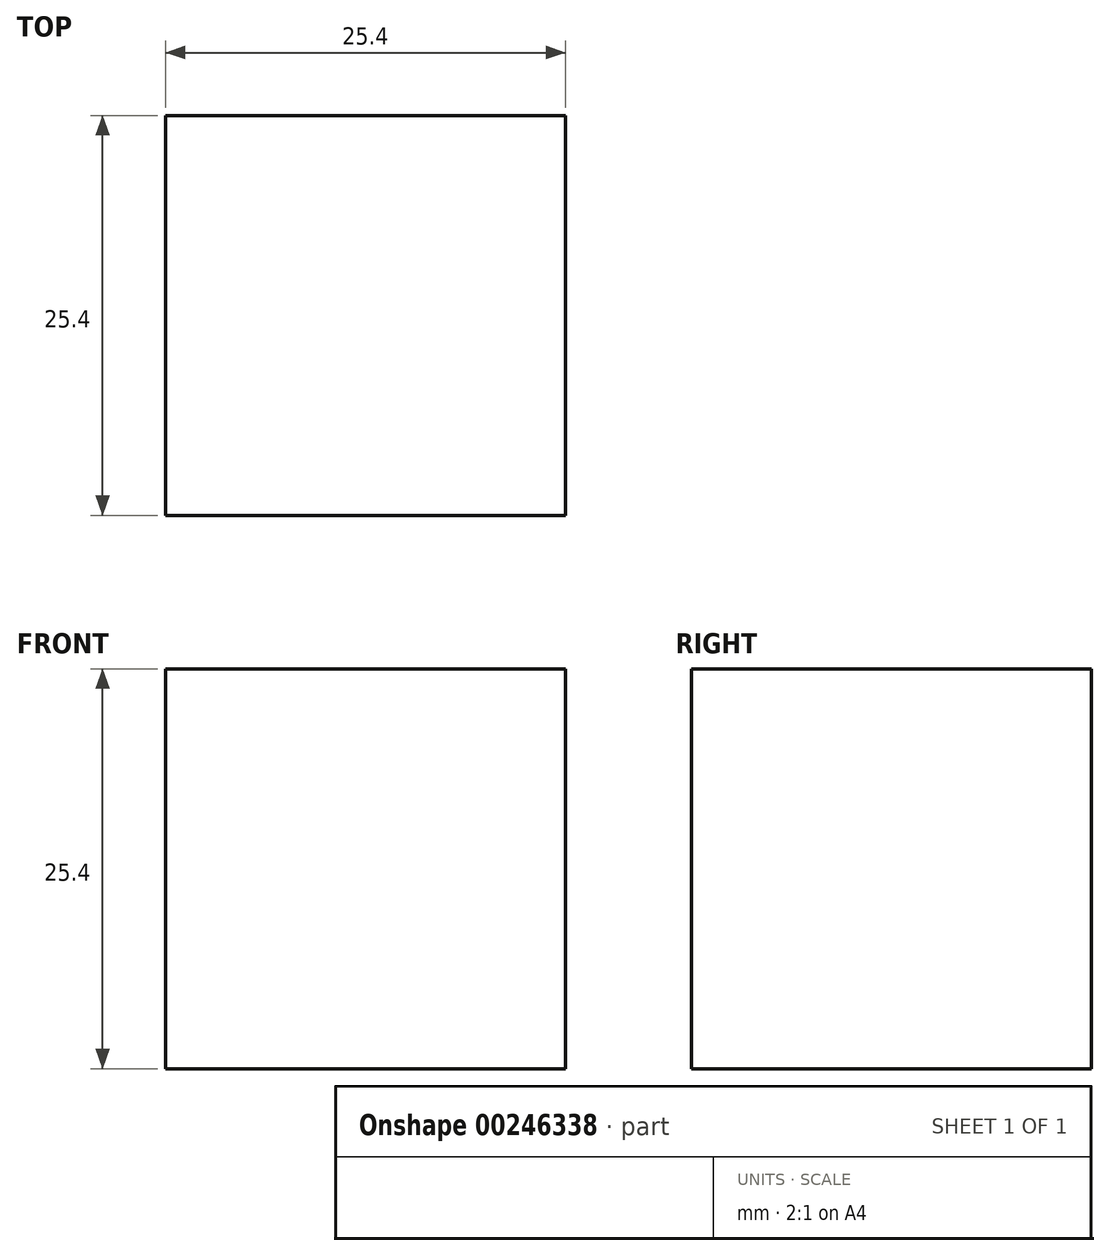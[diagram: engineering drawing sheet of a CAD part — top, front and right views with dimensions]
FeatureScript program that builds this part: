
annotation { "Feature Type Name" : "Feature", "Feature Type Description" : "" }
export const myFeature = defineFeature(function(context is Context, id is Id, definition is map)
    precondition{}
    {
        {
            var Q0;
            Q0=qCreatedBy(makeId("Front.planeOp"),FACE);
            var sketch = newSketch(context, id + "F0", { "sketchPlane" : qUnion([Q0])});
            skLineSegment(sketch, "E0.bottom", {"start": v(-35.63, -10.53) * mm, "end": v(-10.23, -10.53) * mm});
            skLineSegment(sketch, "E0.top", {"start": v(-35.63, -35.93) * mm, "end": v(-10.23, -35.93) * mm});
            skLineSegment(sketch, "E0.left", {"start": v(-35.63, -10.53) * mm, "end": v(-35.63, -35.93) * mm});
            skLineSegment(sketch, "E0.right", {"start": v(-10.23, -10.53) * mm, "end": v(-10.23, -35.93) * mm});
            skSolve(sketch);
        }
        {
            var Q0;
            Q0 = qSketchRegion(id + "F0", true);
            extrude(context, id + "F1", {"entities" : qUnion([Q0]), "depth" : 25.4 * mm});
        }
    });
